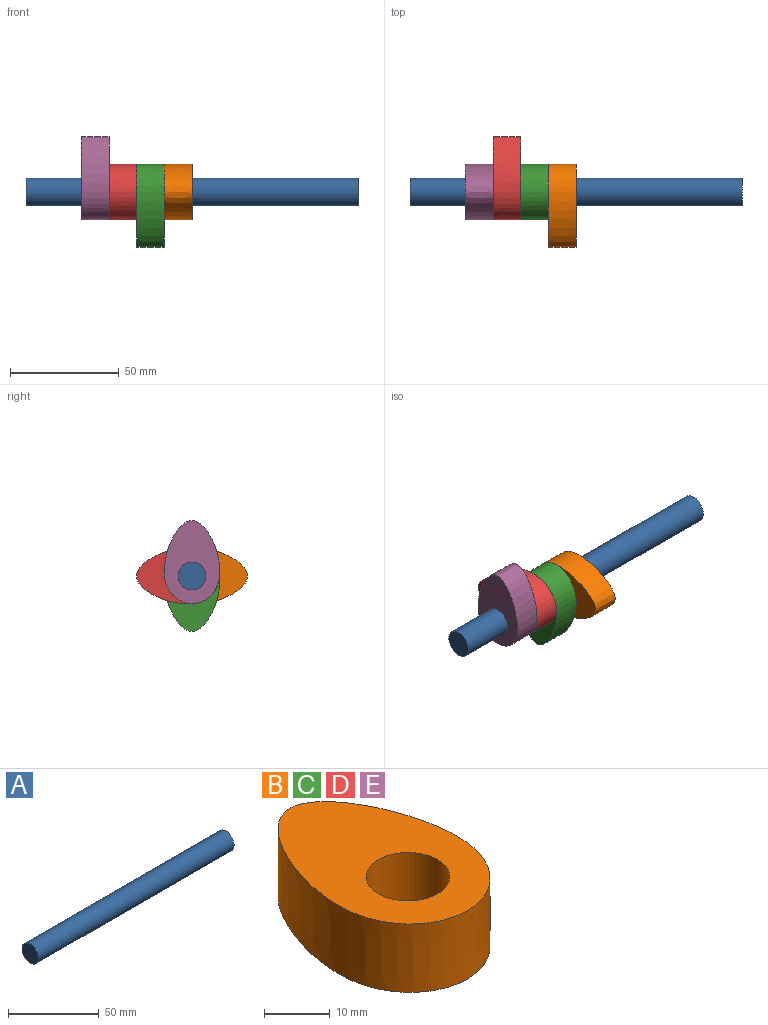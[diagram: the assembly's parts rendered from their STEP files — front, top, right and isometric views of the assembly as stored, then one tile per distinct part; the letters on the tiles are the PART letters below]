
ASSEMBLY  parts=5 mates=4
PART A: 3 faces, bbox 152.4x12.7x12.7 mm
  f0: cylinder r=6.35mm len=152.4mm, axis (-1,0,0), area 6080.5mm2, adj f1,f2
  f1: plane 12.7x12.7mm, normal (1,0,0), area 126.7mm2, adj f0
  f2: plane 12.7x12.7mm, normal (-1,0,0), area 126.7mm2, adj f0
PART B: 4 faces, bbox 28.4x41.1x12.7 mm
  f0: extruded ~38.09x25.58mm, area 1275.8mm2, adj f2,f3
  f1: cylinder r=6.35mm len=12.7mm, axis (0,0,-1), area 506.7mm2, adj f2,f3
  f2: plane 41.09x28.39mm, normal (0,0,1), area 620.1mm2, adj f0,f1
  f3: plane 41.09x28.39mm, normal (0,0,-1), area 620.1mm2, adj f0,f1
PART C: same geometry as B
PART D: same geometry as B
PART E: same geometry as B
PLACE A at identity fixed
PLACE B rot(axis=(0.71,0,0.71),180deg) t=(-12.7,0,0)mm
PLACE C rot(axis=(-0.58,0.58,-0.58),120deg) t=(-25.4,0,0)mm
PLACE D rot(axis=(0,-1,0),90deg) t=(-25.4,0,0)mm
PLACE E rot(axis=(0.58,-0.58,-0.58),120deg) t=(-38.1,0,0)mm
MATE fastened C.f1 <-> D.f1  axis (-1,0,0) through (-25.4,0,0)mm
MATE fastened C.f1 <-> B.f1  axis (-1,0,0) through (-12.7,0,0)mm
MATE fastened D.f1 <-> E.f1  axis (-1,0,0) through (-38.1,0,0)mm
MATE fastened A.f0 <-> B.f1  axis (-1,0,0) through (0,0,0)mm
